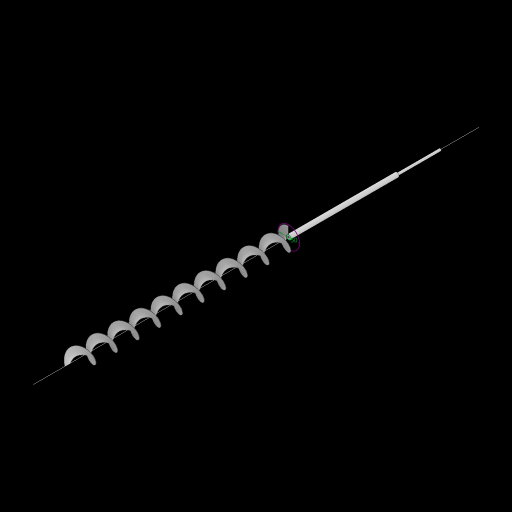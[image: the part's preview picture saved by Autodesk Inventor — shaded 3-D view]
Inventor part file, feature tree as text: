
AUTODESK INVENTOR PART (.ipt)
format: ipt  version: 2023 (Build 270158000, 158)  size: 344,064 bytes
history: native  units: mm
features: sketch x4, extrude x2, helix x1
ambient origin geometry x8: Origin, YZ Plane, XZ Plane, XY Plane, X Axis, Y Axis, Z Axis, Center Point
bodies: Solid1 (feature_tree)
feature tree (7):
  extrude  "Extrusion1"  Depth=250.0mm TaperAngle=0.0deg
  extrude  "Extrusion2"  Depth=100.0mm TaperAngle=0.0deg
  sketch  "Sketch3"  dims[d7=50.0mm d8=500.0mm d9=50.0mm d10=0.0mm d11=90.0deg d12=90.0deg d13=0.0mm d14=0.0mm]
  helix  "Coil1"  [1 undecoded]
  sketch  "Sketch1"  dims[d0=10.0mm d1=250.0mm d2=0.0mm]
  sketch  "Sketch2"  dims[d3=5.0mm d4=100.0mm d5=0.0mm d6=50.0mm]
  sketch  "Sketch4"
note: 1 required parameter value undecoded (feature->parameter linkage not recoverable at this tier; creation-order binding heuristic only, values carry confidence <= 0.55)
